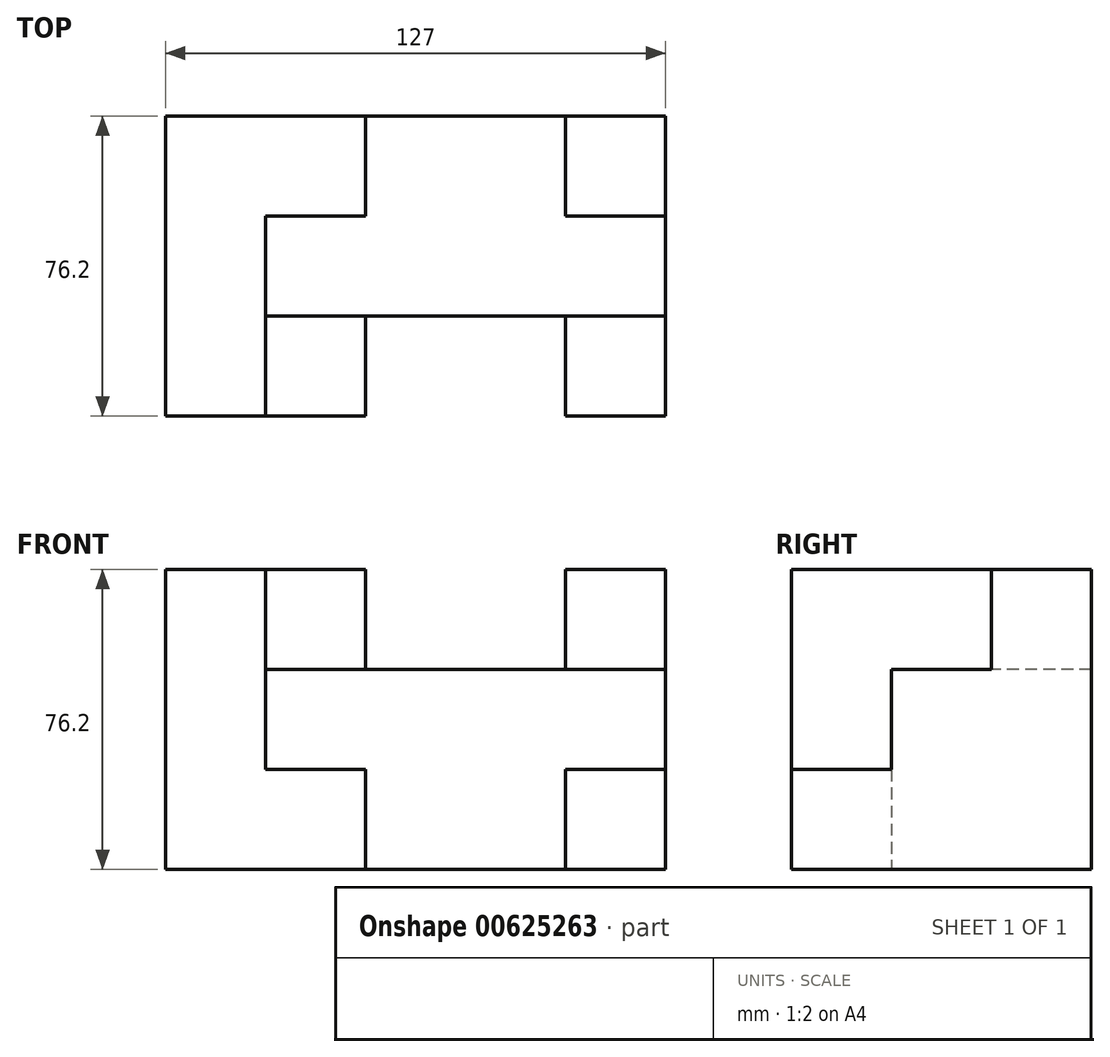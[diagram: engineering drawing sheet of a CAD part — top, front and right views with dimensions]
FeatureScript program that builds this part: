
annotation { "Feature Type Name" : "Feature", "Feature Type Description" : "" }
export const myFeature = defineFeature(function(context is Context, id is Id, definition is map)
    precondition{}
    {
        {
            var Q0;
            Q0=qCreatedBy(makeId("Front.planeOp"),FACE);
            var sketch = newSketch(context, id + "F0", { "sketchPlane" : qUnion([Q0])});
            skLineSegment(sketch, "E0.bottom", {"start": v(-53.05, 14.44) * mm, "end": v(73.95, 14.44) * mm});
            skLineSegment(sketch, "E0.top", {"start": v(-53.05, -61.76) * mm, "end": v(73.95, -61.76) * mm});
            skLineSegment(sketch, "E0.left", {"start": v(-53.05, 14.44) * mm, "end": v(-53.05, -61.76) * mm});
            skLineSegment(sketch, "E0.right", {"start": v(73.95, 14.44) * mm, "end": v(73.95, -61.76) * mm});
            skSolve(sketch);
        }
        {
            var Q0;
            Q0=makeQuery(id+"F0.imprint","IMPRINT",FACE,{"disambiguationData":[TD([[makeQuery(id+"F0.imprint","IMPRINT",EDGE,{"derivedFrom":sQuery(id+"F0.wireOp",EDGE,"E0.bottom")}),-1.0]])]});
            extrude(context, id + "F1", {"entities" : qUnion([Q0]), "depth" : 76.2 * mm, "offsetDistance" : 25.4 * mm});
        }
        {
            var Q0;
            Q0=makeQuery(id+"F1.opExtrude","CAP_FACE",FACE,{"disambiguationData":[OSD([sQuery(id+"F0.wireOp",EDGE,"E0.bottom"),sQuery(id+"F0.wireOp",EDGE,"E0.top"),sQuery(id+"F0.wireOp",EDGE,"E0.left"),sQuery(id+"F0.wireOp",EDGE,"E0.right")])],"isStart":false});
            var sketch = newSketch(context, id + "F2", { "sketchPlane" : qUnion([Q0])});
            skLineSegment(sketch, "E1", {"start": v(-53.05, 18.8) * mm, "end": v(-2.25, 18.8) * mm});
            skLineSegment(sketch, "E2", {"start": v(-2.25, 18.8) * mm, "end": v(-2.25, -10.96) * mm});
            skLineSegment(sketch, "E3", {"start": v(48.55, 14.66) * mm, "end": v(48.55, -10.96) * mm});
            skLineSegment(sketch, "E4", {"start": v(48.55, -10.96) * mm, "end": v(78, -10.96) * mm});
            skLineSegment(sketch, "E5", {"start": v(78.85, -36.36) * mm, "end": v(48.55, -36.36) * mm});
            skLineSegment(sketch, "E6", {"start": v(48.55, -36.36) * mm, "end": v(48.55, -63.1) * mm});
            skLineSegment(sketch, "E7", {"start": v(48.55, -36.36) * mm, "end": v(-2.25, -36.36) * mm});
            skLineSegment(sketch, "E8", {"start": v(-2.25, -36.36) * mm, "end": v(-27.65, -36.36) * mm});
            skLineSegment(sketch, "E9", {"start": v(-27.65, -36.36) * mm, "end": v(-27.65, 18.8) * mm});
            skLineSegment(sketch, "E10", {"start": v(-2.25, -10.96) * mm, "end": v(-27.65, -10.96) * mm});
            skLineSegment(sketch, "E11", {"start": v(-2.25, -36.36) * mm, "end": v(-2.25, -62.77) * mm});
            skLineSegment(sketch, "E12", {"start": v(-2.25, -10.96) * mm, "end": v(48.55, -10.96) * mm});
            skSolve(sketch);
        }
        {
            var Q0;
            {var subQ0=sQuery(id+"F2.wireOp",EDGE,"E2");Q0=makeQuery(id+"F2.imprint","IMPRINT",FACE,{"disambiguationData":[TD([[makeQuery(id+"F2.imprint","IMPRINT",EDGE,{"derivedFrom":subQ0}),-1.0]])]});}
            var Q1;
            {var subQ0=sQuery(id+"F2.wireOp",EDGE,"E4");var subQ1=sQuery(id+"F2.wireOp",EDGE,"E3");var subQ2=makeQuery(id+"F2.imprint","INTERSECT",VERTEX,{"derivedFrom":[subQ1,subQ0]});Q1=makeQuery(id+"F2.imprint","IMPRINT",FACE,{"disambiguationData":[TD([[makeQuery(id+"F2.imprint","IMPRINT",EDGE,{"disambiguationData":[TD([[subQ2,1.0]])],"derivedFrom":subQ1}),1.0]])]});}
            extrude(context, id + "F3", {"entities" : qUnion([Q0, Q1]), "operationType" : NewBodyOperationType.REMOVE, "oppositeDirection" : true, "depth" : 50.8 * mm, "offsetDistance" : 25.4 * mm});
        }
        {
            var Q0;
            {var subQ0=sQuery(id+"F2.wireOp",EDGE,"E12");Q0=makeQuery(id+"F2.imprint","IMPRINT",FACE,{"disambiguationData":[TD([[makeQuery(id+"F2.imprint","IMPRINT",EDGE,{"derivedFrom":subQ0}),1.0]])]});}
            extrude(context, id + "F4", {"entities" : qUnion([Q0]), "operationType" : NewBodyOperationType.REMOVE, "endBound" : BoundingType.THROUGH_ALL, "oppositeDirection" : true, "depth" : 25.4 * mm, "offsetDistance" : 25.4 * mm});
        }
        {
            var Q0;
            {var subQ1=sQuery(id+"F2.wireOp",EDGE,"E7");Q0=makeQuery(id+"F2.imprint","IMPRINT",FACE,{"disambiguationData":[TD([[makeQuery(id+"F2.imprint","IMPRINT",EDGE,{"derivedFrom":subQ1}),-1.0]])]});}
            var Q1;
            {var subQ0=sQuery(id+"F2.wireOp",EDGE,"E7");Q1=makeQuery(id+"F2.imprint","IMPRINT",FACE,{"disambiguationData":[TD([[makeQuery(id+"F2.imprint","IMPRINT",EDGE,{"derivedFrom":subQ0}),1.0]])]});}
            extrude(context, id + "F5", {"entities" : qUnion([Q0, Q1]), "operationType" : NewBodyOperationType.REMOVE, "oppositeDirection" : true, "depth" : 25.4 * mm, "offsetDistance" : 25.4 * mm});
        }
    });
